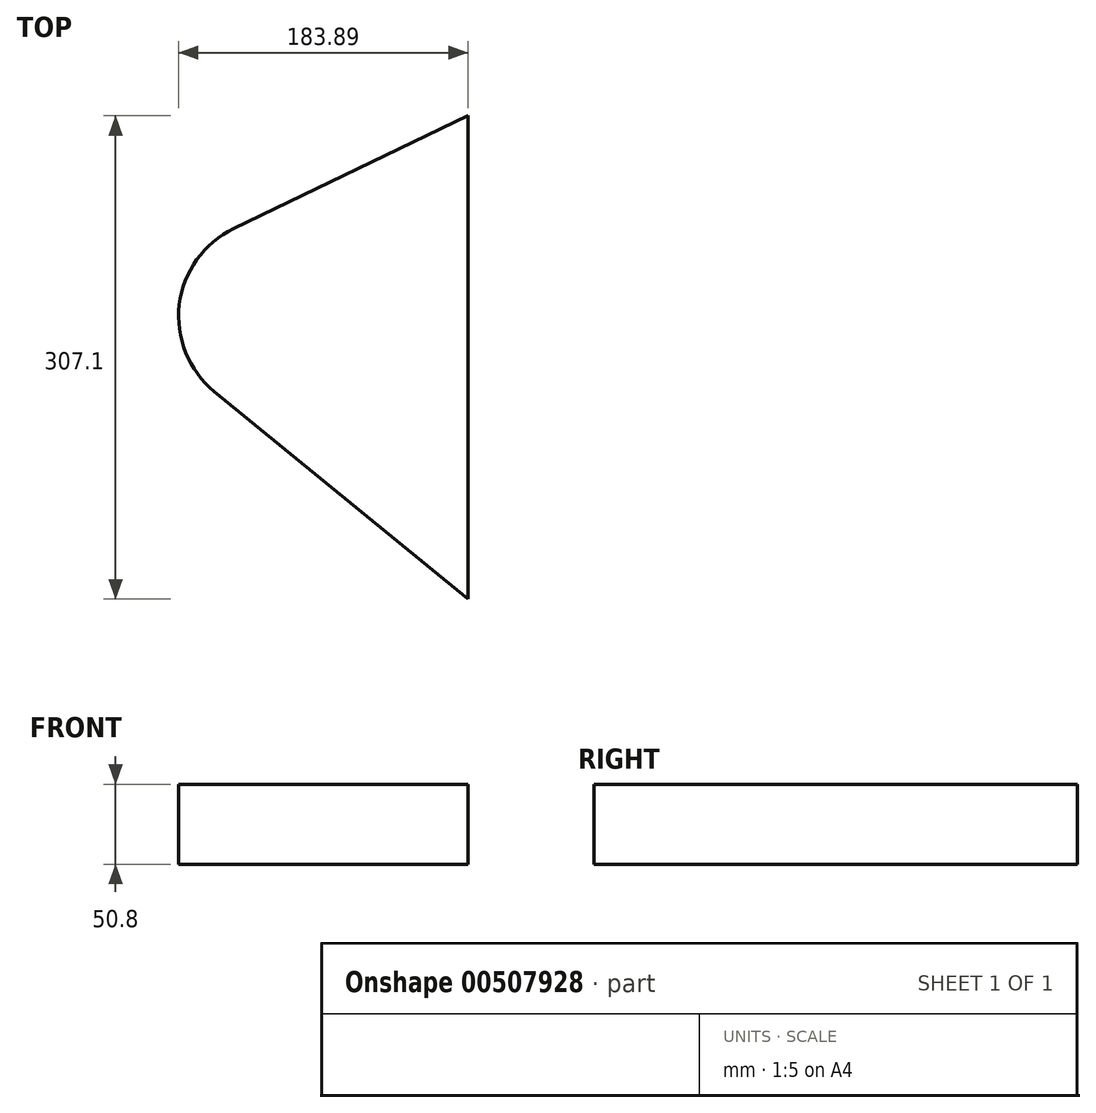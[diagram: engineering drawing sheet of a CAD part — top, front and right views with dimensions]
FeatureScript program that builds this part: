
annotation { "Feature Type Name" : "Feature", "Feature Type Description" : "" }
export const myFeature = defineFeature(function(context is Context, id is Id, definition is map)
    precondition{}
    {
        {
            var Q0;
            Q0=qCreatedBy(makeId("Top.planeOp"),FACE);
            var sketch = newSketch(context, id + "F0", { "sketchPlane" : qUnion([Q0])});
            skArc(sketch, "E0", {"start": v(-26.8, 55.7) * mm, "mid": v(-61.37, 7.3) * mm, "end": v(-39.14, -47.84) * mm});
            skLineSegment(sketch, "E1", {"start": v(-39.14, -47.84) * mm, "end": v(122.08, -179.73) * mm});
            skLineSegment(sketch, "E2", {"start": v(122.08, -179.73) * mm, "end": v(122.08, 127.37) * mm});
            skLineSegment(sketch, "E3", {"start": v(122.08, 127.37) * mm, "end": v(-26.8, 55.7) * mm});
            skSolve(sketch);
        }
        {
            var Q0;
            Q0=makeQuery(id+"F0.imprint","IMPRINT",FACE,{"disambiguationData":[TD([[makeQuery(id+"F0.imprint","IMPRINT",EDGE,{"derivedFrom":sQuery(id+"F0.wireOp",EDGE,"E0")}),1.0]])]});
            extrude(context, id + "F1", {"entities" : qUnion([Q0]), "depth" : 50.8 * mm});
        }
    });
